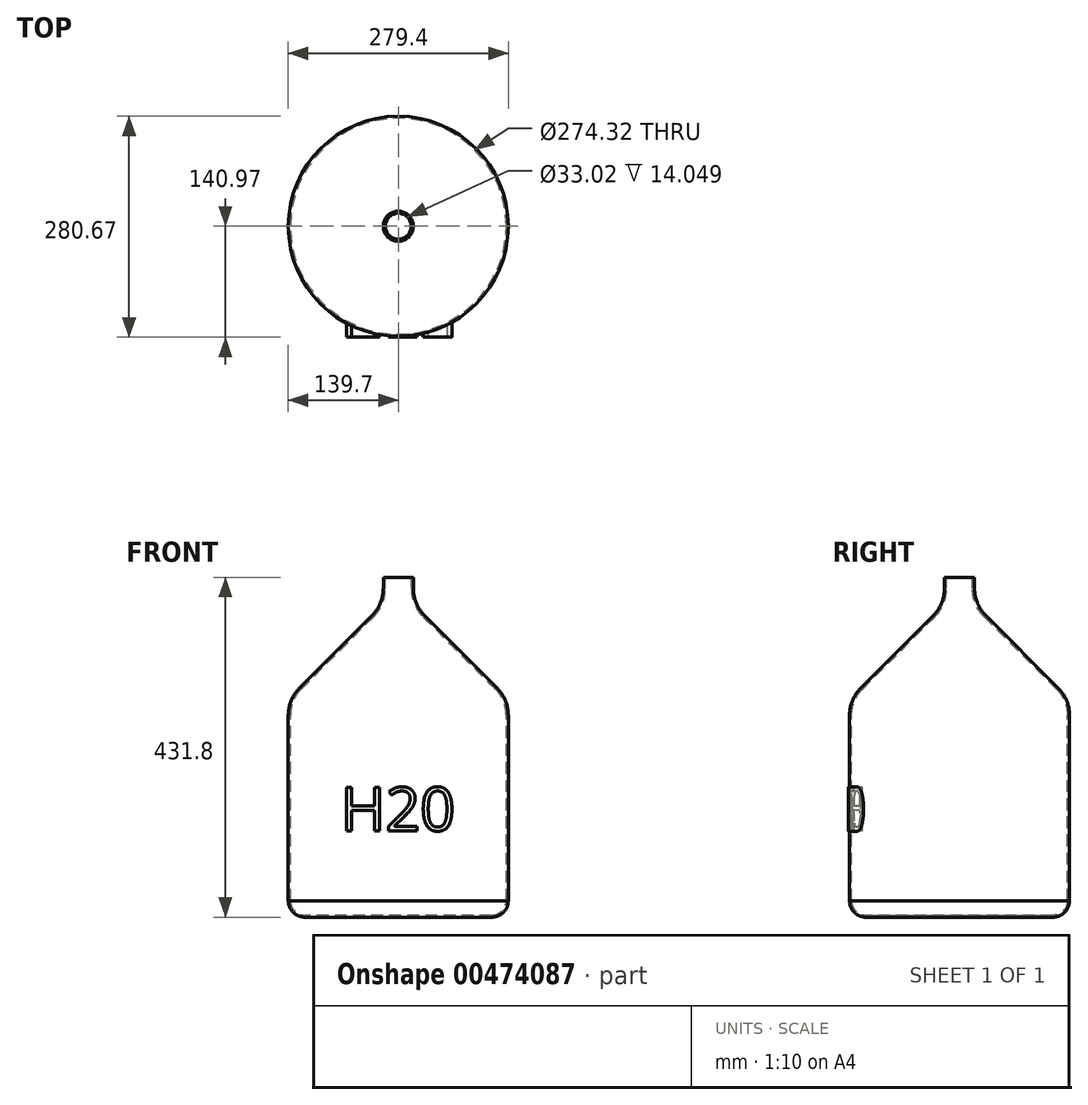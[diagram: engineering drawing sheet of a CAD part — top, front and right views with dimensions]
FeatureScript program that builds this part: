
annotation { "Feature Type Name" : "Feature", "Feature Type Description" : "" }
export const myFeature = defineFeature(function(context is Context, id is Id, definition is map)
    precondition{}
    {
        {
            var Q0;
            Q0=qCreatedBy(makeId("Front.planeOp"),FACE);
            var sketch = newSketch(context, id + "F0", { "sketchPlane" : qUnion([Q0])});
            skLineSegment(sketch, "E0", {"start": v(0, 0) * mm, "end": v(118.49, 0) * mm});
            skArc(sketch, "E1", {"start": v(118.49, 0) * mm, "mid": v(133.4, 6.13) * mm, "end": v(139.7, 20.97) * mm});
            skLineSegment(sketch, "E2", {"start": v(139.7, 20.97) * mm, "end": v(139.7, 256.5) * mm});
            skLineSegment(sketch, "E3", {"start": v(19.05, 431.8) * mm, "end": v(0, 431.8) * mm});
            skLineSegment(sketch, "E4", {"start": v(0, 431.8) * mm, "end": v(0, 0) * mm});
            skLineSegment(sketch, "E5", {"start": v(19.05, 431.8) * mm, "end": v(19.05, 417.75) * mm});
            skArc(sketch, "E6", {"start": v(19.05, 417.75) * mm, "mid": v(22.75, 399.13) * mm, "end": v(33.3, 383.35) * mm});
            skArc(sketch, "E7", {"start": v(139.7, 256.5) * mm, "mid": v(135.94, 275.4) * mm, "end": v(125.24, 291.41) * mm});
            skLineSegment(sketch, "E8", {"start": v(33.3, 383.35) * mm, "end": v(125.24, 291.41) * mm});
            skSolve(sketch);
        }
        {
            var Q0;
            Q0=makeQuery(id+"F0.imprint","IMPRINT",FACE,{"disambiguationData":[TD([[makeQuery(id+"F0.imprint","IMPRINT",EDGE,{"derivedFrom":sQuery(id+"F0.wireOp",EDGE,"E0")}),1.0]])]});
            var Q1;
            Q1=sQuery(id+"F0.wireOp",EDGE,"E4");
            revolve(context, id + "F1", {"entities" : qUnion([Q0]), "axis" : qUnion([Q1]), "revolveType" : RevolveType.FULL});
        }
        {
            var Q0;
            Q0=makeQuery(id+"F1.opRevolve","SWEPT_FACE",FACE,{"disambiguationData":[OSD([sQuery(id+"F0.wireOp",EDGE,"E3")])]});
            shell(context, id + "F2", {"entities" : qUnion([Q0]), "thickness" : 2.54 * mm});
        }
        {
            var Q0;
            Q0=qCreatedBy(makeId("Front.planeOp"),FACE);
            cPlane(context, id + "F3", {"entities" : qUnion([Q0]), "cplaneType" : CPlaneType.OFFSET, "offset" : 140.97 * mm, "width" : 152.4 * mm, "height" : 152.4 * mm});
        }
        {
            var Q0;
            Q0=qCreatedBy(id+"F3.planeOp",FACE);
            var sketch = newSketch(context, id + "F4", { "sketchPlane" : qUnion([Q0])});
            skText(sketch, "E9", { "text": "H20\n", "fontName": "OpenSans-Regular.ttf"});
            const initialGuessF4  = {"E9": [-0.07313, 0.10983, 1, 0, 0.05553]};
            skSetInitialGuess(sketch, initialGuessF4);
            skSolve(sketch);
        }
        {
            var Q0;
            Q0 = qSketchRegion(id + "F4", true);
            var Q1;
            Q1=makeQuery(id+"F1.opRevolve","SWEPT_FACE",FACE,{"disambiguationData":[OSD([sQuery(id+"F0.wireOp",EDGE,"E2")])]});
            var Q2;
            Q2=makeQuery(id+"F1.opRevolve","SWEPT_BODY",BODY,{"disambiguationData":[OSD([sQuery(id+"F0.wireOp",EDGE,"E0"),sQuery(id+"F0.wireOp",EDGE,"E1"),sQuery(id+"F0.wireOp",EDGE,"E2"),sQuery(id+"F0.wireOp",EDGE,"326eb4ac-e30a-4731-96ef-aa0775514d7b"),sQuery(id+"F0.wireOp",EDGE,"E3"),sQuery(id+"F0.wireOp",EDGE,"E4"),sQuery(id+"F0.wireOp",EDGE,"E5"),sQuery(id+"F0.wireOp",EDGE,"f0af26b4-111a-4f23-9503-0cbd4206f02f")])]});
            extrude(context, id + "F5", {"entities" : qUnion([Q0]), "operationType" : NewBodyOperationType.ADD, "endBound" : BoundingType.UP_TO_SURFACE, "oppositeDirection" : true, "endBoundEntityFace" : qUnion([Q1]), "endBoundEntityBody" : qUnion([Q2]), "depth" : 25.4 * mm});
        }
    });
